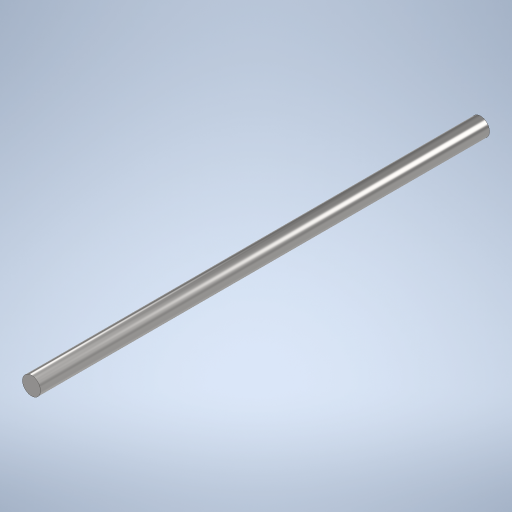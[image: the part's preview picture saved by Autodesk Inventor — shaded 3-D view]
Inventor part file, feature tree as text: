
AUTODESK INVENTOR PART (.ipt)
format: ipt  version: 2023.2 (Build 272271000, 271)  size: 266,752 bytes
history: native  units: mm
features: extrude x1, sketch x1
ambient origin geometry x8: Origin, YZ Plane, XZ Plane, XY Plane, X Axis, Y Axis, Z Axis, Center Point
bodies: Solid1 (feature_tree)
feature tree (2):
  extrude  "Extrusion1"  Depth=300.0mm TaperAngle=0.0deg
  sketch  "Sketch1"  dims[d0=12.0mm d1=300.0mm d2=0.0mm d5=0.5mm d6=0.872665mm d7=0.5mm d8=0.872665mm]
